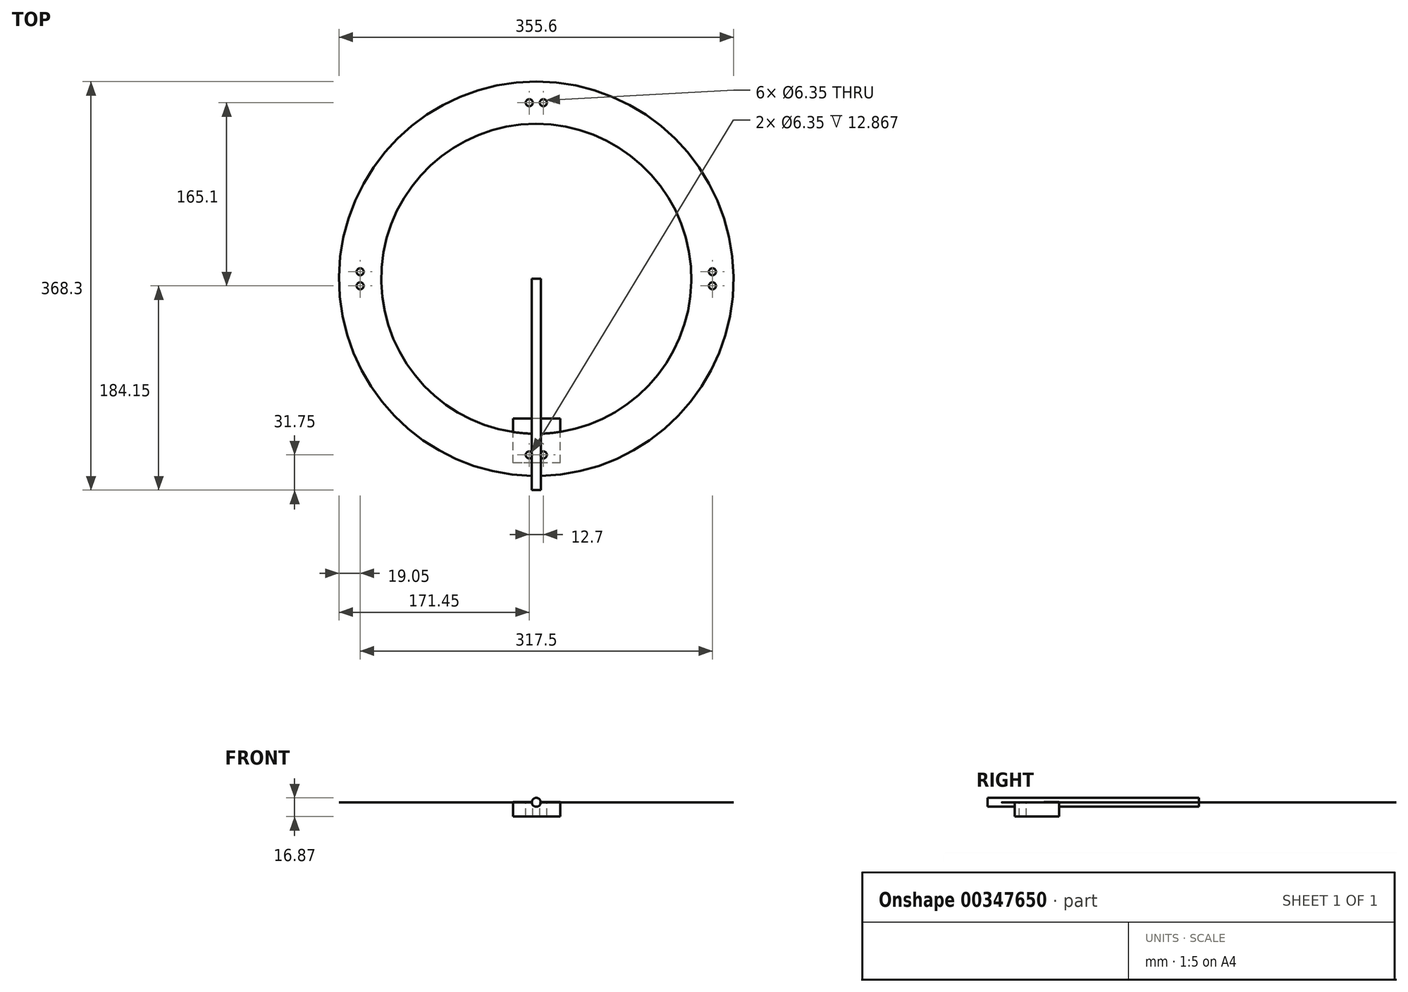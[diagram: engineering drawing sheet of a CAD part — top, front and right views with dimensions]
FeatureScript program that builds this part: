
annotation { "Feature Type Name" : "Feature", "Feature Type Description" : "" }
export const myFeature = defineFeature(function(context is Context, id is Id, definition is map)
    precondition{}
    {
        {
            assignVariable(context, id + "F0", {"name" : "Material_Thickness", "anyValue" : .167});
        }
        {
            var Q0;
            Q0=qCreatedBy(makeId("Top.planeOp"),FACE);
            var sketch = newSketch(context, id + "F1", { "sketchPlane" : qUnion([Q0])});
            skCircle(sketch, "E0", {"center": v(0, 0) * mm, "radius": 177.8 * mm});
            skCircle(sketch, "E1", {"center": v(0, 0) * mm, "radius": 139.7 * mm});
            skSolve(sketch);
        }
        {
            var Q0;
            Q0=makeQuery(id+"F1.imprint","IMPRINT",FACE,{"disambiguationData":[TD([[makeQuery(id+"F1.imprint","IMPRINT",EDGE,{"derivedFrom":sQuery(id+"F1.wireOp",EDGE,"E0")}),1.0]])]});
            extrude(context, id + "F2", {"entities" : qUnion([Q0]), "oppositeDirection" : true, "depth" : (getVariable(context, 'Material_Thickness')) * mm});
        }
        {
            var Q0;
            Q0=qCreatedBy(makeId("Front.planeOp"),FACE);
            var sketch = newSketch(context, id + "F3", { "sketchPlane" : qUnion([Q0])});
            skCircle(sketch, "E2", {"center": v(0, 0) * mm, "radius": 4 * mm});
            skSolve(sketch);
        }
        {
            var Q0;
            Q0 = qSketchRegion(id + "F3", true);
            extrude(context, id + "F4", {"entities" : qUnion([Q0]), "depth" : 190.5 * mm});
        }
        {
            var Q0;
            Q0=makeQuery(id+"F2.opExtrude","CAP_FACE",FACE,{"disambiguationData":[OSD([sQuery(id+"F1.wireOp",EDGE,"E0"),sQuery(id+"F1.wireOp",EDGE,"E1")])],"isStart":true});
            var sketch = newSketch(context, id + "F5", { "sketchPlane" : qUnion([Q0])});
            skCircle(sketch, "E3", {"center": v(-6.35, 158.75) * mm, "radius": 3.18 * mm});
            skCircle(sketch, "E4", {"center": v(6.35, 158.75) * mm, "radius": 3.18 * mm});
            skLineSegment(sketch, "E5", {"start": v(-6.35, 158.75) * mm, "end": v(6.35, 158.75) * mm});
            skLineSegment(sketch, "E6", {"start": v(0, 158.75) * mm, "end": v(0, 0) * mm});
            skCircle(sketch, "E7.1.0", {"center": v(-158.75, -6.35) * mm, "radius": 3.18 * mm});
            skCircle(sketch, "E7.1.1", {"center": v(-158.75, 6.35) * mm, "radius": 3.18 * mm});
            skCircle(sketch, "E7.2.0", {"center": v(6.35, -158.75) * mm, "radius": 3.18 * mm});
            skCircle(sketch, "E7.2.1", {"center": v(-6.35, -158.75) * mm, "radius": 3.18 * mm});
            skCircle(sketch, "E7.3.0", {"center": v(158.75, 6.35) * mm, "radius": 3.18 * mm});
            skCircle(sketch, "E7.3.1", {"center": v(158.75, -6.35) * mm, "radius": 3.18 * mm});
            skPoint(sketch, "E7.center", {"position": v(0, 0) * mm});
            skSolve(sketch);
        }
        {
            var Q0;
            Q0=makeQuery(id+"F5.imprint","IMPRINT",FACE,{"disambiguationData":[TD([[makeQuery(id+"F5.imprint","IMPRINT",EDGE,{"derivedFrom":sQuery(id+"F5.wireOp",EDGE,"E3")}),1.0]])]});
            var Q1;
            Q1=makeQuery(id+"F5.imprint","IMPRINT",FACE,{"disambiguationData":[TD([[makeQuery(id+"F5.imprint","IMPRINT",EDGE,{"derivedFrom":sQuery(id+"F5.wireOp",EDGE,"E4")}),1.0]])]});
            var Q2;
            Q2=makeQuery(id+"F5.imprint","IMPRINT",FACE,{"disambiguationData":[TD([[makeQuery(id+"F5.imprint","IMPRINT",EDGE,{"derivedFrom":sQuery(id+"F5.wireOp",EDGE,"E7.1.1")}),1.0]])]});
            var Q3;
            Q3=makeQuery(id+"F5.imprint","IMPRINT",FACE,{"disambiguationData":[TD([[makeQuery(id+"F5.imprint","IMPRINT",EDGE,{"derivedFrom":sQuery(id+"F5.wireOp",EDGE,"E7.1.0")}),1.0]])]});
            var Q4;
            Q4=makeQuery(id+"F5.imprint","IMPRINT",FACE,{"disambiguationData":[TD([[makeQuery(id+"F5.imprint","IMPRINT",EDGE,{"derivedFrom":sQuery(id+"F5.wireOp",EDGE,"E7.2.1")}),1.0]])]});
            var Q5;
            Q5=makeQuery(id+"F5.imprint","IMPRINT",FACE,{"disambiguationData":[TD([[makeQuery(id+"F5.imprint","IMPRINT",EDGE,{"derivedFrom":sQuery(id+"F5.wireOp",EDGE,"E7.2.0")}),1.0]])]});
            var Q6;
            Q6=makeQuery(id+"F5.imprint","IMPRINT",FACE,{"disambiguationData":[TD([[makeQuery(id+"F5.imprint","IMPRINT",EDGE,{"derivedFrom":sQuery(id+"F5.wireOp",EDGE,"E7.3.1")}),1.0]])]});
            var Q7;
            Q7=makeQuery(id+"F5.imprint","IMPRINT",FACE,{"disambiguationData":[TD([[makeQuery(id+"F5.imprint","IMPRINT",EDGE,{"derivedFrom":sQuery(id+"F5.wireOp",EDGE,"E7.3.0")}),1.0]])]});
            extrude(context, id + "F6", {"entities" : qUnion([Q0, Q1, Q2, Q3, Q4, Q5, Q6, Q7]), "operationType" : NewBodyOperationType.REMOVE, "oppositeDirection" : true, "depth" : 25.4 * mm});
        }
        {
            var Q0;
            Q0=makeQuery(id+"F2.opExtrude","CAP_FACE",FACE,{"disambiguationData":[OSD([sQuery(id+"F1.wireOp",EDGE,"E0"),sQuery(id+"F1.wireOp",EDGE,"E1")])],"isStart":false});
            var sketch = newSketch(context, id + "F7", { "sketchPlane" : qUnion([Q0])});
            skLineSegment(sketch, "E8.bottom", {"start": v(21.68, 166.12) * mm, "end": v(-21.01, 166.12) * mm});
            skLineSegment(sketch, "E8.top", {"start": v(21.68, 125.98) * mm, "end": v(-21.01, 125.98) * mm});
            skLineSegment(sketch, "E8.left", {"start": v(21.68, 166.12) * mm, "end": v(21.68, 125.98) * mm});
            skLineSegment(sketch, "E8.right", {"start": v(-21.01, 166.12) * mm, "end": v(-21.01, 125.98) * mm});
            skSolve(sketch);
        }
        {
            var Q0;
            {var subQ0=sQuery(id+"F7.wireOp",EDGE,"E8.top");Q0=makeQuery(id+"F7.imprint","IMPRINT",FACE,{"disambiguationData":[TD([[makeQuery(id+"F7.imprint","IMPRINT",EDGE,{"derivedFrom":subQ0}),-1.0]])]});}
            var Q1;
            {var subQ2=sQuery(id+"F7.wireOp",EDGE,"E8.bottom");Q1=makeQuery(id+"F7.imprint","IMPRINT",FACE,{"disambiguationData":[TD([[makeQuery(id+"F7.imprint","IMPRINT",EDGE,{"derivedFrom":subQ2}),1.0]])]});}
            extrude(context, id + "F8", {"entities" : qUnion([Q0, Q1]), "depth" : 12.7 * mm});
        }
        {
            var Q0;
            Q0=makeQuery(id+"F8.opExtrude","CAP_FACE",FACE,{"disambiguationData":[OSD([sQuery(id+"F1.wireOp",EDGE,"E0"),sQuery(id+"F1.wireOp",EDGE,"E1"),sQuery(id+"F5.wireOp",EDGE,"E7.2.0"),sQuery(id+"F5.wireOp",EDGE,"E7.2.1"),sQuery(id+"F7.wireOp",EDGE,"E8.bottom"),sQuery(id+"F7.wireOp",EDGE,"E8.top"),sQuery(id+"F7.wireOp",EDGE,"E8.left"),sQuery(id+"F7.wireOp",EDGE,"E8.right")])],"isStart":true});
            var sketch = newSketch(context, id + "F9", { "sketchPlane" : qUnion([Q0])});
            skCircle(sketch, "E9.0", {"center": v(0, 0) * mm, "radius": 139.7 * mm});
            skSolve(sketch);
        }
        {
            var Q0;
            {var subQ5=makeQuery(id+"F8.opExtrude","CAP_EDGE",EDGE,{"disambiguationData":[OSD([sQuery(id+"F7.wireOp",EDGE,"E8.top")])],"isStart":true});Q0=makeQuery(id+"F9.imprint","IMPRINT",FACE,{"disambiguationData":[TD([[makeQuery(id+"F9.imprint","IMPRINT",EDGE,{"derivedFrom":subQ5}),1.0]])]});}
            extrude(context, id + "F10", {"entities" : qUnion([Q0]), "operationType" : NewBodyOperationType.ADD, "depth" : 2 * (getVariable(context, 'Material_Thickness')) * mm});
        }
    });
